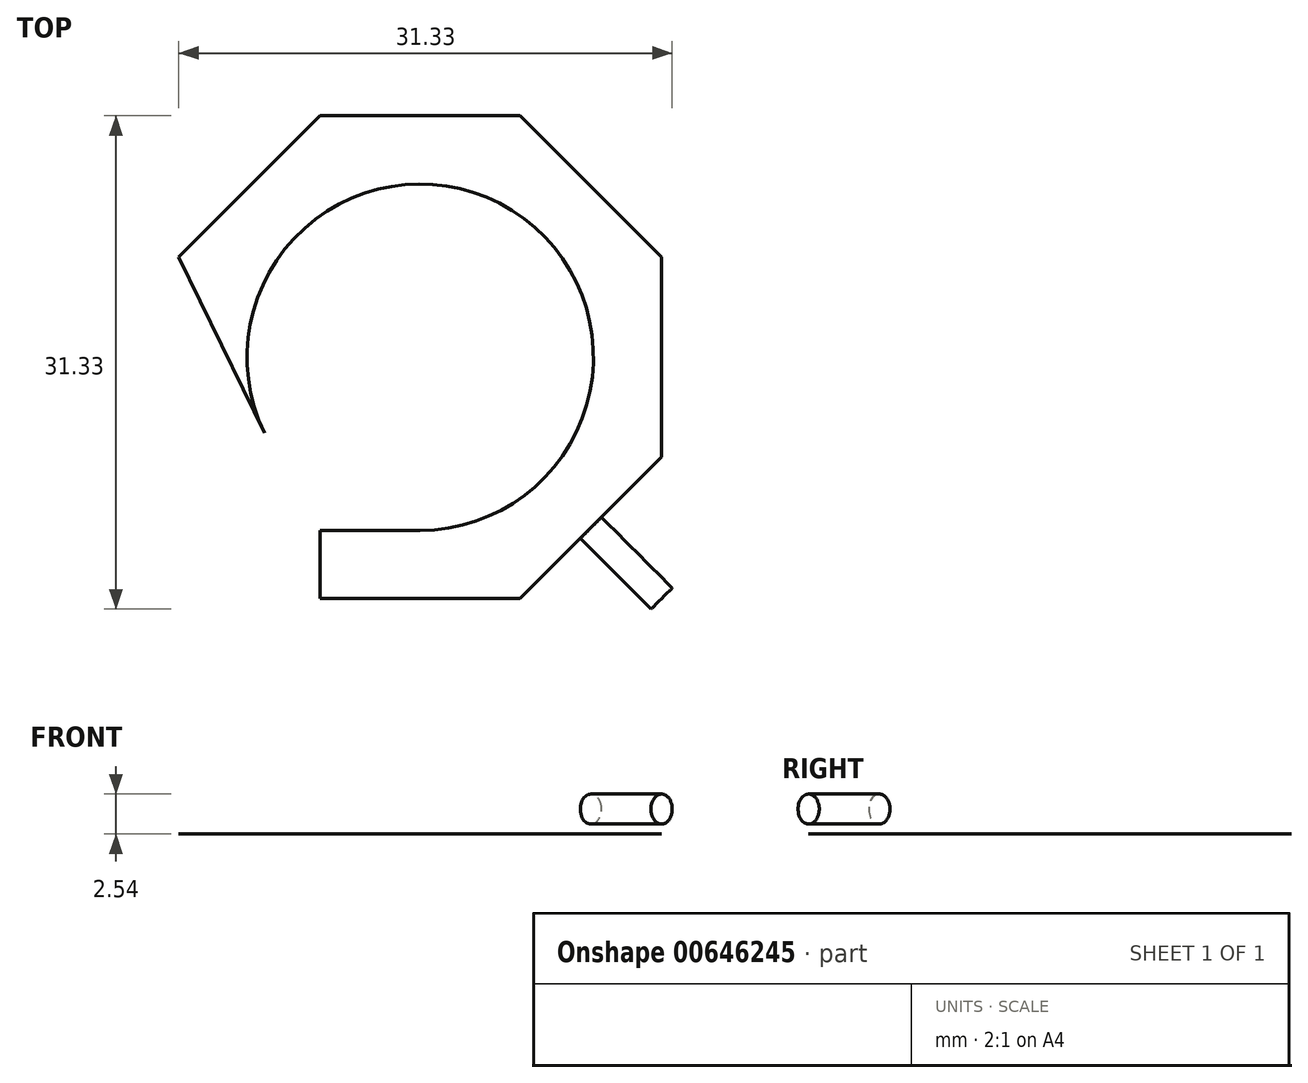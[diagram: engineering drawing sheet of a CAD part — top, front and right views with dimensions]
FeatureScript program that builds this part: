
annotation { "Feature Type Name" : "Feature", "Feature Type Description" : "" }
export const myFeature = defineFeature(function(context is Context, id is Id, definition is map)
    precondition{}
    {
        {
            var Q0;
            Q0=qCreatedBy(makeId("Top.planeOp"),FACE);
            var sketch = newSketch(context, id + "F0", { "sketchPlane" : qUnion([Q0])});
            skLineSegment(sketch, "E0", {"start": v(0, 0) * mm, "end": v(12.7, 0) * mm});
            skLineSegment(sketch, "E1", {"start": v(15.24, 2.54) * mm, "end": v(12.7, 0) * mm});
            skLineSegment(sketch, "E2", {"start": v(12.7, 0) * mm, "end": v(21.68, 8.98) * mm});
            skLineSegment(sketch, "E3", {"start": v(21.68, 8.98) * mm, "end": v(21.68, 21.68) * mm});
            skLineSegment(sketch, "E4", {"start": v(21.68, 21.68) * mm, "end": v(12.7, 30.66) * mm});
            skLineSegment(sketch, "E5", {"start": v(12.7, 30.66) * mm, "end": v(0, 30.66) * mm});
            skPoint(sketch, "E6.center.orphan", {"position": v(6.35, 15.33) * mm});
            skArc(sketch, "E7", {"start": v(6.35, 4.33) * mm, "mid": v(12.18, 24.66) * mm, "end": v(-3.54, 10.51) * mm});
            skPoint(sketch, "E8.start.orphan", {"position": v(0, 2.63) * mm});
            skLineSegment(sketch, "E9", {"start": v(6.35, 4.33) * mm, "end": v(0, 4.33) * mm});
            skLineSegment(sketch, "E10", {"start": v(0, 4.33) * mm, "end": v(0, 0) * mm});
            skLineSegment(sketch, "E11", {"start": v(-2.54, 28.12) * mm, "end": v(0, 30.66) * mm});
            skPoint(sketch, "E12.startSnap0", {"position": v(0, 29.4) * mm});
            skPoint(sketch, "E12.start.orphan", {"position": v(2.76, 29.4) * mm});
            skPoint(sketch, "E13.orphan", {"position": v(0, 28.12) * mm});
            skLineSegment(sketch, "E14", {"start": v(0, 30.66) * mm, "end": v(-8.98, 21.68) * mm});
            skLineSegment(sketch, "E15", {"start": v(-8.98, 21.68) * mm, "end": v(-3.54, 10.51) * mm});
            skSolve(sketch);
        }
        {
            var Q0;
            {var subQ2=sQuery(id+"F0.wireOp",EDGE,"E0");Q0=makeQuery(id+"F0.imprint","IMPRINT",FACE,{"disambiguationData":[TD([[makeQuery(id+"F0.imprint","IMPRINT",EDGE,{"derivedFrom":subQ2}),1.0]])]});}
            extrude(context, id + "F1", {"entities" : qUnion([Q0]), "depth" : 1 / 203.2 * mm, "offsetDistance" : 25.4 * mm});
        }
        {
            var Q0;
            Q0=makeQuery(id+"F1.opExtrude","SWEPT_FACE",FACE,{"disambiguationData":[OSD([sQuery(id+"F0.wireOp",EDGE,"E2")])]});
            var sketch = newSketch(context, id + "F2", { "sketchPlane" : qUnion([Q0])});
            skLineSegment(sketch, "E16", {"start": v(21.68, 0) * mm, "end": v(21.68, 3.18) * mm});
            skCircle(sketch, "E17", {"center": v(15.33, 1.59) * mm, "radius": 0.95 * mm});
            skPoint(sketch, "E18.trimOffspring.end.orphan", {"position": v(8.98, 0) * mm});
            skSolve(sketch);
        }
        {
            var Q0;
            Q0 = qSketchRegion(id + "F2", true);
            extrude(context, id + "F3", {"entities" : qUnion([Q0]), "operationType" : NewBodyOperationType.ADD, "depth" : 6.35 * mm, "offsetDistance" : 25.4 * mm});
        }
    });
